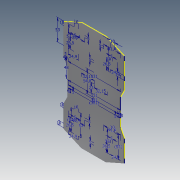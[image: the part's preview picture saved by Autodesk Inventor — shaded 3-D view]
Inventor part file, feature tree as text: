
AUTODESK INVENTOR PART (.ipt)
format: ipt  version: 2013 (Build 170138000, 138)  size: 172,032 bytes
history: native  units: mm
features: sketch x2, extrude x1
ambient origin geometry x8: Origin, YZ Plane, XZ Plane, XY Plane, X Axis, Y Axis, Z Axis, Center Point
bodies: Solid1 (feature_tree)
feature tree (3):
  extrude  "Extrusion1"  Depth=10.0mm
  sketch  "Sketch2"  dims[d27=10.0mm d28=10.0mm d29=53.0mm d30=10.0mm d31=24.9mm d32=53.0mm d33=10.0mm d35=24.9mm d36=10.0mm d37=53.0mm d38=24.9mm d39=53.0mm d40=10.0mm d41=53.0mm d42=24.9mm d43=53.0mm d44=10.0mm d45=53.0mm d47=131.0mm d48=10.0mm d49=131.0mm d50=54.8mm d51=48.0mm d52=131.0mm d53=2.0mm d54=131.0mm d68=5.0mm d70=5.0mm d71=5.0mm d73=5.0mm d74=5.0mm d76=23.0mm d77=32.15mm d78=32.15mm d86=5.0mm d88=5.0mm d90=5.0mm d92=41.4mm d93=5.0mm d94=41.4mm d98=41.4mm d99=5.0mm d100=41.4mm d101=5.0mm d104=26.5mm d105=5.0mm d106=26.5mm d107=5.0mm d108=26.5mm d109=5.0mm d110=26.5mm d111=5.0mm]
  sketch  "Sketch1"  dims[d24=2.0mm d25=0.0mm d26=10.0mm]
